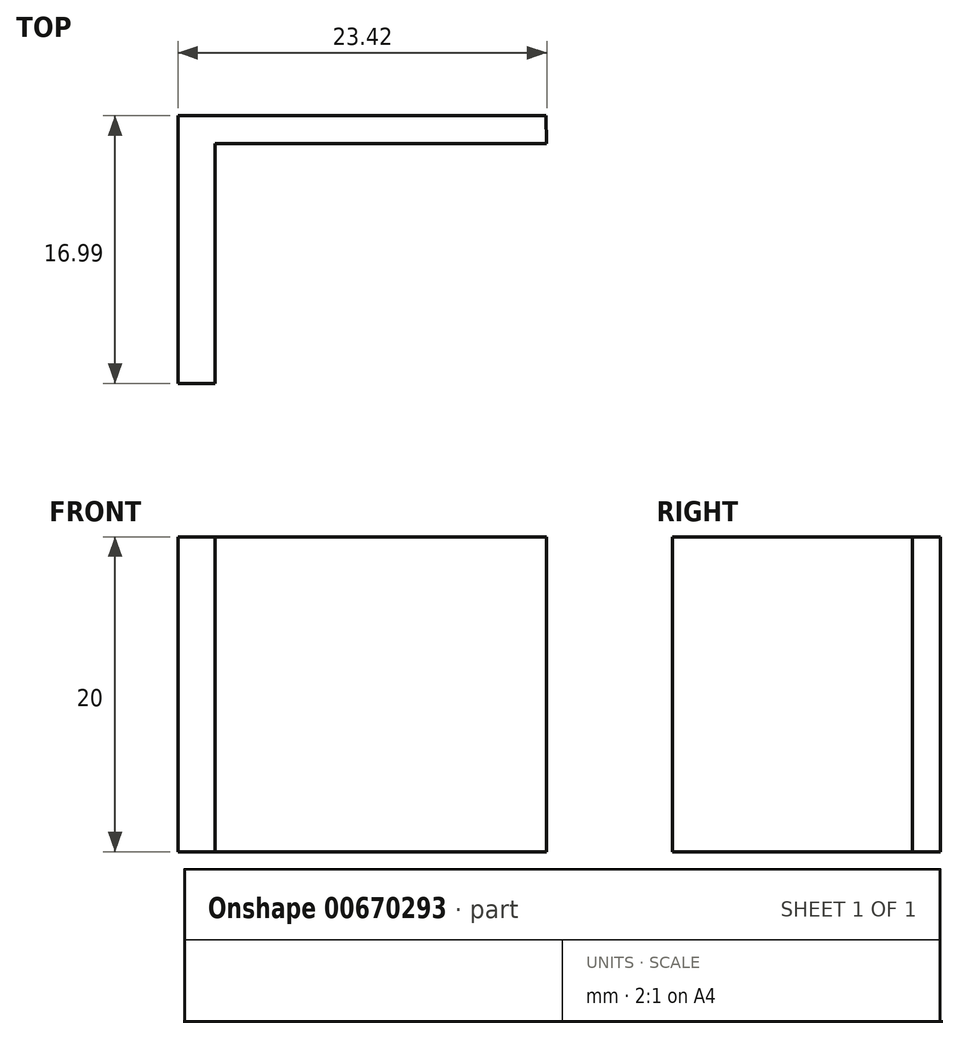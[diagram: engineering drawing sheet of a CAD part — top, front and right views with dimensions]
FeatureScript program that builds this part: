
annotation { "Feature Type Name" : "Feature", "Feature Type Description" : "" }
export const myFeature = defineFeature(function(context is Context, id is Id, definition is map)
    precondition{}
    {
        {
            var Q0;
            Q0=qCreatedBy(makeId("Top.planeOp"),FACE);
            var sketch = newSketch(context, id + "F0", { "sketchPlane" : qUnion([Q0])});
            skLineSegment(sketch, "E0", {"start": v(14.84, 4.49) * mm, "end": v(-6.23, 4.49) * mm});
            skLineSegment(sketch, "E1", {"start": v(-6.23, 4.49) * mm, "end": v(-6.23, -10.74) * mm});
            skLineSegment(sketch, "E2", {"start": v(-8.58, -10.74) * mm, "end": v(-8.58, 6.25) * mm});
            skLineSegment(sketch, "E3", {"start": v(-8.58, 6.25) * mm, "end": v(14.79, 6.25) * mm});
            skLineSegment(sketch, "E4", {"start": v(14.79, 6.25) * mm, "end": v(14.84, 4.49) * mm});
            skLineSegment(sketch, "E5", {"start": v(-6.23, -10.74) * mm, "end": v(-8.58, -10.74) * mm});
            skSolve(sketch);
        }
        {
            var Q0;
            Q0=sQuery(id+"F0.wireOp",EDGE,"E0");
            var Q1;
            Q1=sQuery(id+"F0.wireOp",EDGE,"E1");
            var Q2;
            Q2=sQuery(id+"F0.wireOp",EDGE,"E2");
            var Q3;
            Q3=sQuery(id+"F0.wireOp",EDGE,"E3");
            var Q4;
            Q4=sQuery(id+"F0.wireOp",EDGE,"E4");
            var Q5;
            Q5=sQuery(id+"F0.wireOp",EDGE,"E5");
            extrude(context, id + "F1", {"bodyType" : ToolBodyType.SURFACE, "surfaceEntities" : qUnion([Q0, Q1, Q2, Q3, Q4, Q5]), "depth" : 20 * mm});
        }
    });
